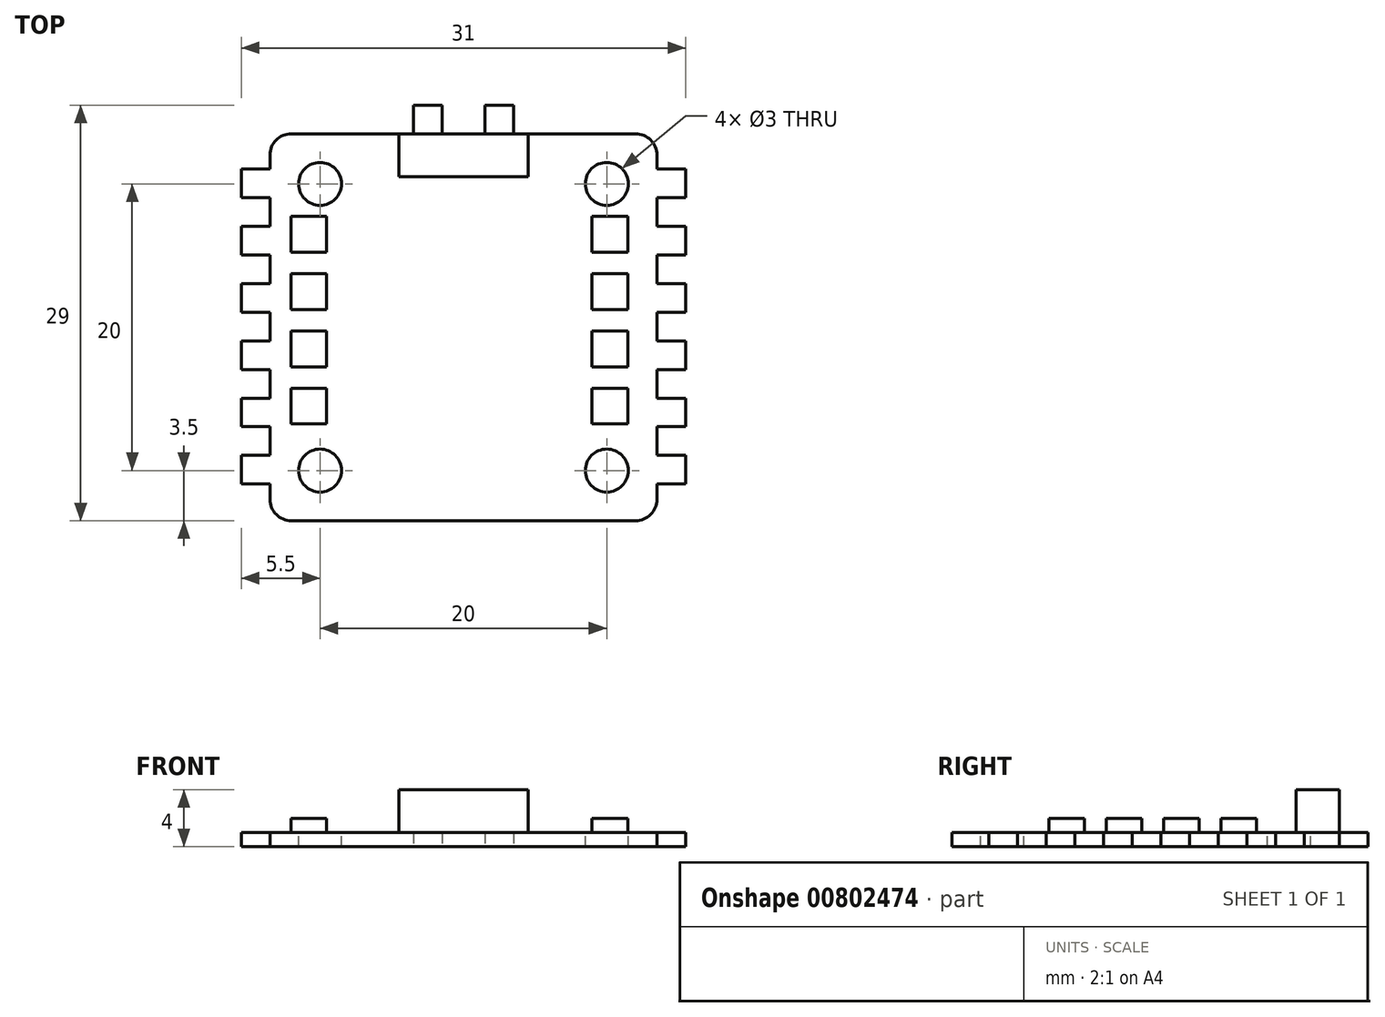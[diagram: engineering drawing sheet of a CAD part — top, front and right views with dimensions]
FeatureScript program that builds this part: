
annotation { "Feature Type Name" : "Feature", "Feature Type Description" : "" }
export const myFeature = defineFeature(function(context is Context, id is Id, definition is map)
    precondition{}
    {
        {
            var Q0;
            Q0=qCreatedBy(makeId("Top.planeOp"),FACE);
            var sketch = newSketch(context, id + "F0", { "sketchPlane" : qUnion([Q0])});
            skLineSegment(sketch, "E0.bottom", {"start": v(-12, 13.5) * mm, "end": v(12, 13.5) * mm});
            skLineSegment(sketch, "E0.top", {"start": v(-12, -13.5) * mm, "end": v(12, -13.5) * mm});
            skLineSegment(sketch, "E0.left", {"start": v(-13.5, 12) * mm, "end": v(-13.5, -12) * mm});
            skLineSegment(sketch, "E0.right", {"start": v(13.5, 12) * mm, "end": v(13.5, -12) * mm});
            skPoint(sketch, "E0.middle", {"position": v(0, 0) * mm});
            skPoint(sketch, "E1.visualSharp", {"position": v(-13.5, 13.5) * mm});
            skArc(sketch, "E1.filletArc", {"start": v(-12, 13.5) * mm, "mid": v(-13.06, 13.06) * mm, "end": v(-13.5, 12) * mm});
            skPoint(sketch, "E2.visualSharp", {"position": v(13.5, 13.5) * mm});
            skArc(sketch, "E2.filletArc", {"start": v(13.5, 12) * mm, "mid": v(13.06, 13.06) * mm, "end": v(12, 13.5) * mm});
            skPoint(sketch, "E3.visualSharp", {"position": v(13.5, -13.5) * mm});
            skArc(sketch, "E3.filletArc", {"start": v(12, -13.5) * mm, "mid": v(13.06, -13.06) * mm, "end": v(13.5, -12) * mm});
            skPoint(sketch, "E4.visualSharp", {"position": v(-13.5, -13.5) * mm});
            skArc(sketch, "E4.filletArc", {"start": v(-13.5, -12) * mm, "mid": v(-13.06, -13.06) * mm, "end": v(-12, -13.5) * mm});
            skLineSegment(sketch, "E5.bottom", {"start": v(-10, 10) * mm, "end": v(10, 10) * mm, "construction": true});
            skLineSegment(sketch, "E5.top", {"start": v(-10, -10) * mm, "end": v(10, -10) * mm, "construction": true});
            skLineSegment(sketch, "E5.left", {"start": v(-10, 10) * mm, "end": v(-10, -10) * mm, "construction": true});
            skLineSegment(sketch, "E5.right", {"start": v(10, 10) * mm, "end": v(10, -10) * mm, "construction": true});
            skPoint(sketch, "E6", {"position": v(-10, 10) * mm});
            skPoint(sketch, "E7", {"position": v(10, 10) * mm});
            skPoint(sketch, "E8", {"position": v(10, -10) * mm});
            skPoint(sketch, "E9", {"position": v(-10, -10) * mm});
            skSolve(sketch);
        }
        {
            var Q0;
            Q0=makeQuery(id+"F0.imprint","IMPRINT",FACE,{"disambiguationData":[TD([[makeQuery(id+"F0.imprint","IMPRINT",EDGE,{"derivedFrom":sQuery(id+"F0.wireOp",EDGE,"E0.bottom")}),-1.0]])]});
            extrude(context, id + "F1", {"entities" : qUnion([Q0]), "oppositeDirection" : true, "depth" : 1 * mm, "offsetDistance" : 25 * mm});
        }
        {
            var Q0;
            Q0=sQuery(id+"F0.wireOp",VERTEX,"E6");
            var Q1;
            Q1=sQuery(id+"F0.wireOp",VERTEX,"E7");
            var Q2;
            Q2=sQuery(id+"F0.wireOp",VERTEX,"E8");
            var Q3;
            Q3=sQuery(id+"F0.wireOp",VERTEX,"E9");
            var Q4;
            Q4=makeQuery(id+"F1.opExtrude","SWEPT_BODY",BODY,{"disambiguationData":[OSD([sQuery(id+"F0.wireOp",EDGE,"E0.bottom"),sQuery(id+"F0.wireOp",EDGE,"E0.top"),sQuery(id+"F0.wireOp",EDGE,"E0.left"),sQuery(id+"F0.wireOp",EDGE,"E0.right"),sQuery(id+"F0.wireOp",EDGE,"E1.filletArc"),sQuery(id+"F0.wireOp",EDGE,"E2.filletArc"),sQuery(id+"F0.wireOp",EDGE,"E3.filletArc"),sQuery(id+"F0.wireOp",EDGE,"E4.filletArc")])]});
            hole(context, id + "F2", {"style" : HoleStyle.SIMPLE, "endStyle" : HoleEndStyle.BLIND, "holeDiameter" : 3 * mm, "majorDiameter" : 5 * mm, "holeDepth" : 5 * mm, "isTappedThrough" : true, "tappedDepth" : 12 * mm, "tapClearance" : 3, "locations" : qUnion([Q0, Q1, Q2, Q3]), "scope" : qUnion([Q4])});
        }
        {
            var Q0;
            Q0=makeQuery(id+"F1.opExtrude","CAP_FACE",FACE,{"disambiguationData":[OSD([sQuery(id+"F0.wireOp",EDGE,"E0.bottom"),sQuery(id+"F0.wireOp",EDGE,"E0.top"),sQuery(id+"F0.wireOp",EDGE,"E0.left"),sQuery(id+"F0.wireOp",EDGE,"E0.right"),sQuery(id+"F0.wireOp",EDGE,"E1.filletArc"),sQuery(id+"F0.wireOp",EDGE,"E2.filletArc"),sQuery(id+"F0.wireOp",EDGE,"E3.filletArc"),sQuery(id+"F0.wireOp",EDGE,"E4.filletArc")])],"isStart":false});
            var sketch = newSketch(context, id + "F3", { "sketchPlane" : qUnion([Q0])});
            skLineSegment(sketch, "E10.bottom", {"start": v(-13.5, 10.94) * mm, "end": v(-15.5, 10.94) * mm});
            skLineSegment(sketch, "E10.top", {"start": v(-13.5, 8.94) * mm, "end": v(-15.5, 8.94) * mm});
            skLineSegment(sketch, "E10.left", {"start": v(-13.5, 10.94) * mm, "end": v(-13.5, 8.94) * mm});
            skLineSegment(sketch, "E10.right", {"start": v(-15.5, 10.94) * mm, "end": v(-15.5, 8.94) * mm});
            skLineSegment(sketch, "E11.0.1.0", {"start": v(-13.5, 6.94) * mm, "end": v(-15.5, 6.94) * mm});
            skLineSegment(sketch, "E11.0.1.1", {"start": v(-13.5, 4.94) * mm, "end": v(-15.5, 4.94) * mm});
            skLineSegment(sketch, "E11.0.1.2", {"start": v(-13.5, 6.94) * mm, "end": v(-13.5, 4.94) * mm});
            skLineSegment(sketch, "E11.0.1.3", {"start": v(-15.5, 6.94) * mm, "end": v(-15.5, 4.94) * mm});
            skLineSegment(sketch, "E11.0.2.0", {"start": v(-13.5, 2.94) * mm, "end": v(-15.5, 2.94) * mm});
            skLineSegment(sketch, "E11.0.2.1", {"start": v(-13.5, 0.94) * mm, "end": v(-15.5, 0.94) * mm});
            skLineSegment(sketch, "E11.0.2.2", {"start": v(-13.5, 2.94) * mm, "end": v(-13.5, 0.94) * mm});
            skLineSegment(sketch, "E11.0.2.3", {"start": v(-15.5, 2.94) * mm, "end": v(-15.5, 0.94) * mm});
            skLineSegment(sketch, "E11.0.3.0", {"start": v(-13.5, -1.06) * mm, "end": v(-15.5, -1.06) * mm});
            skLineSegment(sketch, "E11.0.3.1", {"start": v(-13.5, -3.06) * mm, "end": v(-15.5, -3.06) * mm});
            skLineSegment(sketch, "E11.0.3.2", {"start": v(-13.5, -1.06) * mm, "end": v(-13.5, -3.06) * mm});
            skLineSegment(sketch, "E11.0.3.3", {"start": v(-15.5, -1.06) * mm, "end": v(-15.5, -3.06) * mm});
            skLineSegment(sketch, "E11.0.4.0", {"start": v(-13.5, -5.06) * mm, "end": v(-15.5, -5.06) * mm});
            skLineSegment(sketch, "E11.0.4.1", {"start": v(-13.5, -7.06) * mm, "end": v(-15.5, -7.06) * mm});
            skLineSegment(sketch, "E11.0.4.2", {"start": v(-13.5, -5.06) * mm, "end": v(-13.5, -7.06) * mm});
            skLineSegment(sketch, "E11.0.4.3", {"start": v(-15.5, -5.06) * mm, "end": v(-15.5, -7.06) * mm});
            skLineSegment(sketch, "E11.0.5.0", {"start": v(-13.5, -9.06) * mm, "end": v(-15.5, -9.06) * mm});
            skLineSegment(sketch, "E11.0.5.1", {"start": v(-13.5, -11.06) * mm, "end": v(-15.5, -11.06) * mm});
            skLineSegment(sketch, "E11.0.5.2", {"start": v(-13.5, -9.06) * mm, "end": v(-13.5, -11.06) * mm});
            skLineSegment(sketch, "E11.0.5.3", {"start": v(-15.5, -9.06) * mm, "end": v(-15.5, -11.06) * mm});
            skLineSegment(sketch, "E11.1.0.0", {"start": v(15.5, 10.94) * mm, "end": v(13.5, 10.94) * mm});
            skLineSegment(sketch, "E11.1.0.1", {"start": v(15.5, 8.94) * mm, "end": v(13.5, 8.94) * mm});
            skLineSegment(sketch, "E11.1.0.2", {"start": v(15.5, 10.94) * mm, "end": v(15.5, 8.94) * mm});
            skLineSegment(sketch, "E11.1.0.3", {"start": v(13.5, 10.94) * mm, "end": v(13.5, 8.94) * mm});
            skLineSegment(sketch, "E11.1.1.0", {"start": v(15.5, 6.94) * mm, "end": v(13.5, 6.94) * mm});
            skLineSegment(sketch, "E11.1.1.1", {"start": v(15.5, 4.94) * mm, "end": v(13.5, 4.94) * mm});
            skLineSegment(sketch, "E11.1.1.2", {"start": v(15.5, 6.94) * mm, "end": v(15.5, 4.94) * mm});
            skLineSegment(sketch, "E11.1.1.3", {"start": v(13.5, 6.94) * mm, "end": v(13.5, 4.94) * mm});
            skLineSegment(sketch, "E11.1.2.0", {"start": v(15.5, 2.94) * mm, "end": v(13.5, 2.94) * mm});
            skLineSegment(sketch, "E11.1.2.1", {"start": v(15.5, 0.94) * mm, "end": v(13.5, 0.94) * mm});
            skLineSegment(sketch, "E11.1.2.2", {"start": v(15.5, 2.94) * mm, "end": v(15.5, 0.94) * mm});
            skLineSegment(sketch, "E11.1.2.3", {"start": v(13.5, 2.94) * mm, "end": v(13.5, 0.94) * mm});
            skLineSegment(sketch, "E11.1.3.0", {"start": v(15.5, -1.06) * mm, "end": v(13.5, -1.06) * mm});
            skLineSegment(sketch, "E11.1.3.1", {"start": v(15.5, -3.06) * mm, "end": v(13.5, -3.06) * mm});
            skLineSegment(sketch, "E11.1.3.2", {"start": v(15.5, -1.06) * mm, "end": v(15.5, -3.06) * mm});
            skLineSegment(sketch, "E11.1.3.3", {"start": v(13.5, -1.06) * mm, "end": v(13.5, -3.06) * mm});
            skLineSegment(sketch, "E11.1.4.0", {"start": v(15.5, -5.06) * mm, "end": v(13.5, -5.06) * mm});
            skLineSegment(sketch, "E11.1.4.1", {"start": v(15.5, -7.06) * mm, "end": v(13.5, -7.06) * mm});
            skLineSegment(sketch, "E11.1.4.2", {"start": v(15.5, -5.06) * mm, "end": v(15.5, -7.06) * mm});
            skLineSegment(sketch, "E11.1.4.3", {"start": v(13.5, -5.06) * mm, "end": v(13.5, -7.06) * mm});
            skLineSegment(sketch, "E11.1.5.0", {"start": v(15.5, -9.06) * mm, "end": v(13.5, -9.06) * mm});
            skLineSegment(sketch, "E11.1.5.1", {"start": v(15.5, -11.06) * mm, "end": v(13.5, -11.06) * mm});
            skLineSegment(sketch, "E11.1.5.2", {"start": v(15.5, -9.06) * mm, "end": v(15.5, -11.06) * mm});
            skLineSegment(sketch, "E11.1.5.3", {"start": v(13.5, -9.06) * mm, "end": v(13.5, -11.06) * mm});
            skLineSegment(sketch, "E11.direction1", {"start": v(-15.5, 8.94) * mm, "end": v(13.5, 8.94) * mm, "construction": true});
            skLineSegment(sketch, "E11.direction2", {"start": v(-15.5, 8.94) * mm, "end": v(-15.5, 4.94) * mm, "construction": true});
            skLineSegment(sketch, "E12.bottom", {"start": v(-1.5, -13.5) * mm, "end": v(-3.5, -13.5) * mm});
            skLineSegment(sketch, "E12.top", {"start": v(-1.5, -15.5) * mm, "end": v(-3.5, -15.5) * mm});
            skLineSegment(sketch, "E12.left", {"start": v(-1.5, -13.5) * mm, "end": v(-1.5, -15.5) * mm});
            skLineSegment(sketch, "E12.right", {"start": v(-3.5, -13.5) * mm, "end": v(-3.5, -15.5) * mm});
            skLineSegment(sketch, "E13.MirrorCS", {"start": v(1.5, -13.5) * mm, "end": v(3.5, -13.5) * mm});
            skLineSegment(sketch, "E14.MirrorCS", {"start": v(1.5, -15.5) * mm, "end": v(3.5, -15.5) * mm});
            skLineSegment(sketch, "E15.MirrorCS", {"start": v(3.5, -13.5) * mm, "end": v(3.5, -15.5) * mm});
            skLineSegment(sketch, "E16.MirrorCS", {"start": v(1.5, -13.5) * mm, "end": v(1.5, -15.5) * mm});
            skSolve(sketch);
        }
        {
            var Q0;
            Q0=makeQuery(id+"F3.imprint","IMPRINT",FACE,{"disambiguationData":[TD([[makeQuery(id+"F3.imprint","IMPRINT",EDGE,{"derivedFrom":sQuery(id+"F3.wireOp",EDGE,"E10.bottom")}),1.0]])]});
            var Q1;
            Q1=makeQuery(id+"F3.imprint","IMPRINT",FACE,{"disambiguationData":[TD([[makeQuery(id+"F3.imprint","IMPRINT",EDGE,{"derivedFrom":sQuery(id+"F3.wireOp",EDGE,"E11.0.1.0")}),1.0]])]});
            var Q2;
            Q2=makeQuery(id+"F3.imprint","IMPRINT",FACE,{"disambiguationData":[TD([[makeQuery(id+"F3.imprint","IMPRINT",EDGE,{"derivedFrom":sQuery(id+"F3.wireOp",EDGE,"E11.0.2.0")}),1.0]])]});
            var Q3;
            Q3=makeQuery(id+"F3.imprint","IMPRINT",FACE,{"disambiguationData":[TD([[makeQuery(id+"F3.imprint","IMPRINT",EDGE,{"derivedFrom":sQuery(id+"F3.wireOp",EDGE,"E11.0.3.0")}),1.0]])]});
            var Q4;
            Q4=makeQuery(id+"F3.imprint","IMPRINT",FACE,{"disambiguationData":[TD([[makeQuery(id+"F3.imprint","IMPRINT",EDGE,{"derivedFrom":sQuery(id+"F3.wireOp",EDGE,"E11.0.4.0")}),1.0]])]});
            var Q5;
            Q5=makeQuery(id+"F3.imprint","IMPRINT",FACE,{"disambiguationData":[TD([[makeQuery(id+"F3.imprint","IMPRINT",EDGE,{"derivedFrom":sQuery(id+"F3.wireOp",EDGE,"E11.0.5.0")}),1.0]])]});
            var Q6;
            Q6=makeQuery(id+"F3.imprint","IMPRINT",FACE,{"disambiguationData":[TD([[makeQuery(id+"F3.imprint","IMPRINT",EDGE,{"derivedFrom":sQuery(id+"F3.wireOp",EDGE,"E11.1.0.0")}),1.0]])]});
            var Q7;
            Q7=makeQuery(id+"F3.imprint","IMPRINT",FACE,{"disambiguationData":[TD([[makeQuery(id+"F3.imprint","IMPRINT",EDGE,{"derivedFrom":sQuery(id+"F3.wireOp",EDGE,"E11.1.1.0")}),1.0]])]});
            var Q8;
            Q8=makeQuery(id+"F3.imprint","IMPRINT",FACE,{"disambiguationData":[TD([[makeQuery(id+"F3.imprint","IMPRINT",EDGE,{"derivedFrom":sQuery(id+"F3.wireOp",EDGE,"E11.1.2.0")}),1.0]])]});
            var Q9;
            Q9=makeQuery(id+"F3.imprint","IMPRINT",FACE,{"disambiguationData":[TD([[makeQuery(id+"F3.imprint","IMPRINT",EDGE,{"derivedFrom":sQuery(id+"F3.wireOp",EDGE,"E11.1.3.0")}),1.0]])]});
            var Q10;
            Q10=makeQuery(id+"F3.imprint","IMPRINT",FACE,{"disambiguationData":[TD([[makeQuery(id+"F3.imprint","IMPRINT",EDGE,{"derivedFrom":sQuery(id+"F3.wireOp",EDGE,"E11.1.4.0")}),1.0]])]});
            var Q11;
            Q11=makeQuery(id+"F3.imprint","IMPRINT",FACE,{"disambiguationData":[TD([[makeQuery(id+"F3.imprint","IMPRINT",EDGE,{"derivedFrom":sQuery(id+"F3.wireOp",EDGE,"E11.1.5.0")}),1.0]])]});
            var Q12;
            Q12=makeQuery(id+"F3.imprint","IMPRINT",FACE,{"disambiguationData":[TD([[makeQuery(id+"F3.imprint","IMPRINT",EDGE,{"derivedFrom":sQuery(id+"F3.wireOp",EDGE,"E12.bottom")}),-1.0]])]});
            var Q13;
            Q13=makeQuery(id+"F3.imprint","IMPRINT",FACE,{"disambiguationData":[TD([[makeQuery(id+"F3.imprint","IMPRINT",EDGE,{"derivedFrom":sQuery(id+"F3.wireOp",EDGE,"E13.MirrorCS")}),-1.0]])]});
            extrude(context, id + "F4", {"entities" : qUnion([Q0, Q1, Q2, Q3, Q4, Q5, Q6, Q7, Q8, Q9, Q10, Q11, Q12, Q13]), "operationType" : NewBodyOperationType.ADD, "oppositeDirection" : true, "depth" : 1 * mm, "offsetDistance" : 25 * mm});
        }
        {
            var Q0;
            Q0=makeQuery(id+"F0.imprint","IMPRINT",FACE,{"disambiguationData":[TD([[makeQuery(id+"F0.imprint","IMPRINT",EDGE,{"derivedFrom":sQuery(id+"F0.wireOp",EDGE,"E0.bottom")}),-1.0]])]});
            var sketch = newSketch(context, id + "F5", { "sketchPlane" : qUnion([Q0])});
            skLineSegment(sketch, "E17.bottom", {"start": v(-4.5, 13.5) * mm, "end": v(4.5, 13.5) * mm});
            skLineSegment(sketch, "E17.top", {"start": v(-4.5, 10.5) * mm, "end": v(4.5, 10.5) * mm});
            skLineSegment(sketch, "E17.left", {"start": v(-4.5, 13.5) * mm, "end": v(-4.5, 10.5) * mm});
            skLineSegment(sketch, "E17.right", {"start": v(4.5, 13.5) * mm, "end": v(4.5, 10.5) * mm});
            skSolve(sketch);
        }
        {
            var Q0;
            Q0=makeQuery(id+"F5.imprint","IMPRINT",FACE,{"disambiguationData":[TD([[makeQuery(id+"F5.imprint","IMPRINT",EDGE,{"derivedFrom":sQuery(id+"F5.wireOp",EDGE,"E17.bottom")}),-1.0]])]});
            extrude(context, id + "F6", {"entities" : qUnion([Q0]), "operationType" : NewBodyOperationType.ADD, "depth" : 3 * mm, "offsetDistance" : 25 * mm});
        }
        {
            var Q0;
            {var subQ0=sQuery(id+"F3.wireOp",EDGE,"E11.1.5.0");var subQ1=sQuery(id+"F3.wireOp",EDGE,"E11.1.4.1");var subQ2=sQuery(id+"F0.wireOp",EDGE,"E2.filletArc");var subQ3=sQuery(id+"F3.wireOp",EDGE,"E11.1.4.0");var subQ4=sQuery(id+"F0.wireOp",EDGE,"E0.left");var subQ5=sQuery(id+"F3.wireOp",EDGE,"E11.1.3.0");var subQ6=sQuery(id+"F3.wireOp",EDGE,"E11.1.2.1");var subQ7=sQuery(id+"F3.wireOp",EDGE,"E11.1.2.0");var subQ8=sQuery(id+"F3.wireOp",EDGE,"E11.1.1.2");var subQ9=sQuery(id+"F3.wireOp",EDGE,"E11.0.5.3");var subQ10=sQuery(id+"F3.wireOp",EDGE,"E11.0.5.1");var subQ11=sQuery(id+"F3.wireOp",EDGE,"E11.0.5.0");var subQ12=sQuery(id+"F3.wireOp",EDGE,"E11.0.4.3");var subQ13=sQuery(id+"F3.wireOp",EDGE,"E11.0.4.1");var subQ14=sQuery(id+"F3.wireOp",EDGE,"E11.0.4.0");var subQ15=sQuery(id+"F3.wireOp",EDGE,"E11.0.3.3");var subQ16=sQuery(id+"F3.wireOp",EDGE,"E11.0.3.1");var subQ17=sQuery(id+"F3.wireOp",EDGE,"E11.1.1.1");var subQ18=sQuery(id+"F0.wireOp",EDGE,"E4.filletArc");var subQ19=sQuery(id+"F3.wireOp",EDGE,"E11.0.1.1");var subQ20=sQuery(id+"F0.wireOp",EDGE,"E3.filletArc");var subQ21=sQuery(id+"F3.wireOp",EDGE,"E11.1.4.2");var subQ22=sQuery(id+"F3.wireOp",EDGE,"E11.0.1.0");var subQ23=sQuery(id+"F3.wireOp",EDGE,"E11.1.0.0");var subQ24=sQuery(id+"F0.wireOp",EDGE,"E0.bottom");var subQ25=sQuery(id+"F3.wireOp",EDGE,"E10.bottom");var subQ26=sQuery(id+"F3.wireOp",EDGE,"E11.1.1.0");var subQ27=sQuery(id+"F0.wireOp",EDGE,"E1.filletArc");var subQ28=sQuery(id+"F3.wireOp",EDGE,"E11.1.2.2");var subQ29=sQuery(id+"F3.wireOp",EDGE,"E10.right");var subQ30=sQuery(id+"F3.wireOp",EDGE,"E11.0.2.0");var subQ31=sQuery(id+"F3.wireOp",EDGE,"E11.1.0.1");var subQ32=sQuery(id+"F0.wireOp",EDGE,"E0.top");var subQ33=sQuery(id+"F3.wireOp",EDGE,"E10.top");var subQ34=sQuery(id+"F3.wireOp",EDGE,"E11.1.0.2");var subQ35=sQuery(id+"F3.wireOp",EDGE,"E11.1.3.1");var subQ36=sQuery(id+"F3.wireOp",EDGE,"E11.1.3.2");var subQ37=sQuery(id+"F3.wireOp",EDGE,"E11.0.1.3");var subQ38=sQuery(id+"F0.wireOp",EDGE,"E0.right");var subQ39=sQuery(id+"F3.wireOp",EDGE,"E11.0.2.1");var subQ40=sQuery(id+"F3.wireOp",EDGE,"E11.0.2.3");var subQ41=sQuery(id+"F3.wireOp",EDGE,"E11.0.3.0");var subQ42=sQuery(id+"F3.wireOp",EDGE,"E11.1.5.1");var subQ43=sQuery(id+"F3.wireOp",EDGE,"E11.1.5.2");Q0=makeQuery(id+"F6.boolean.opBoolean","SPLIT",FACE,{"disambiguationData":[TD([makeQuery(id+"F1.opExtrude","SWEPT_FACE",FACE,{"disambiguationData":[OSD([subQ32])]})])],"derivedFrom":makeQuery(id+"F4.boolean.opBoolean","MERGE",FACE,{"derivedFrom":[makeQuery(id+"F1.opExtrude","CAP_FACE",FACE,{"disambiguationData":[OSD([subQ24,subQ32,subQ4,subQ38,subQ27,subQ2,subQ20,subQ18])],"isStart":true}),makeQuery(id+"F4.opExtrude","CAP_FACE",FACE,{"disambiguationData":[OSD([subQ25,subQ33,sQuery(id+"F3.wireOp",EDGE,"E10.left"),subQ29])],"isStart":false}),makeQuery(id+"F4.opExtrude","CAP_FACE",FACE,{"disambiguationData":[OSD([subQ22,subQ19,sQuery(id+"F3.wireOp",EDGE,"E11.0.1.2"),subQ37])],"isStart":false}),makeQuery(id+"F4.opExtrude","CAP_FACE",FACE,{"disambiguationData":[OSD([subQ30,subQ39,sQuery(id+"F3.wireOp",EDGE,"E11.0.2.2"),subQ40])],"isStart":false}),makeQuery(id+"F4.opExtrude","CAP_FACE",FACE,{"disambiguationData":[OSD([subQ41,subQ16,sQuery(id+"F3.wireOp",EDGE,"E11.0.3.2"),subQ15])],"isStart":false}),makeQuery(id+"F4.opExtrude","CAP_FACE",FACE,{"disambiguationData":[OSD([subQ14,subQ13,sQuery(id+"F3.wireOp",EDGE,"E11.0.4.2"),subQ12])],"isStart":false}),makeQuery(id+"F4.opExtrude","CAP_FACE",FACE,{"disambiguationData":[OSD([subQ11,subQ10,sQuery(id+"F3.wireOp",EDGE,"E11.0.5.2"),subQ9])],"isStart":false}),makeQuery(id+"F4.opExtrude","CAP_FACE",FACE,{"disambiguationData":[OSD([subQ23,subQ31,subQ34,sQuery(id+"F3.wireOp",EDGE,"E11.1.0.3")])],"isStart":false}),makeQuery(id+"F4.opExtrude","CAP_FACE",FACE,{"disambiguationData":[OSD([subQ26,subQ17,subQ8,sQuery(id+"F3.wireOp",EDGE,"E11.1.1.3")])],"isStart":false}),makeQuery(id+"F4.opExtrude","CAP_FACE",FACE,{"disambiguationData":[OSD([subQ7,subQ6,subQ28,sQuery(id+"F3.wireOp",EDGE,"E11.1.2.3")])],"isStart":false}),makeQuery(id+"F4.opExtrude","CAP_FACE",FACE,{"disambiguationData":[OSD([subQ5,subQ35,subQ36,sQuery(id+"F3.wireOp",EDGE,"E11.1.3.3")])],"isStart":false}),makeQuery(id+"F4.opExtrude","CAP_FACE",FACE,{"disambiguationData":[OSD([subQ3,subQ1,subQ21,sQuery(id+"F3.wireOp",EDGE,"E11.1.4.3")])],"isStart":false}),makeQuery(id+"F4.opExtrude","CAP_FACE",FACE,{"disambiguationData":[OSD([subQ0,subQ42,subQ43,sQuery(id+"F3.wireOp",EDGE,"E11.1.5.3")])],"isStart":false}),makeQuery(id+"F4.opExtrude","CAP_FACE",FACE,{"disambiguationData":[OSD([sQuery(id+"F3.wireOp",EDGE,"E12.bottom"),sQuery(id+"F3.wireOp",EDGE,"E12.top"),sQuery(id+"F3.wireOp",EDGE,"E12.left"),sQuery(id+"F3.wireOp",EDGE,"E12.right")])],"isStart":false}),makeQuery(id+"F4.opExtrude","CAP_FACE",FACE,{"disambiguationData":[OSD([sQuery(id+"F3.wireOp",EDGE,"E13.MirrorCS"),sQuery(id+"F3.wireOp",EDGE,"E14.MirrorCS"),sQuery(id+"F3.wireOp",EDGE,"E15.MirrorCS"),sQuery(id+"F3.wireOp",EDGE,"E16.MirrorCS")])],"isStart":false})]})});}
            var sketch = newSketch(context, id + "F7", { "sketchPlane" : qUnion([Q0])});
            skLineSegment(sketch, "E18.bottom", {"start": v(-9.54, 7.75) * mm, "end": v(-12.04, 7.75) * mm});
            skLineSegment(sketch, "E18.top", {"start": v(-9.54, 5.25) * mm, "end": v(-12.04, 5.25) * mm});
            skLineSegment(sketch, "E18.left", {"start": v(-9.54, 7.75) * mm, "end": v(-9.54, 5.25) * mm});
            skLineSegment(sketch, "E18.right", {"start": v(-12.04, 7.75) * mm, "end": v(-12.04, 5.25) * mm});
            skPoint(sketch, "E18.middle", {"position": v(-10.79, 6.5) * mm});
            skPoint(sketch, "E19.0.1.0", {"position": v(-10.79, 2.5) * mm});
            skLineSegment(sketch, "E19.0.1.1", {"start": v(-12.04, 3.75) * mm, "end": v(-12.04, 1.25) * mm});
            skLineSegment(sketch, "E19.0.1.2", {"start": v(-9.54, 3.75) * mm, "end": v(-9.54, 1.25) * mm});
            skLineSegment(sketch, "E19.0.1.3", {"start": v(-9.54, 1.25) * mm, "end": v(-12.04, 1.25) * mm});
            skLineSegment(sketch, "E19.0.1.4", {"start": v(-9.54, 3.75) * mm, "end": v(-12.04, 3.75) * mm});
            skPoint(sketch, "E19.0.2.0", {"position": v(-10.79, -1.5) * mm});
            skLineSegment(sketch, "E19.0.2.1", {"start": v(-12.04, -0.25) * mm, "end": v(-12.04, -2.75) * mm});
            skLineSegment(sketch, "E19.0.2.2", {"start": v(-9.54, -0.25) * mm, "end": v(-9.54, -2.75) * mm});
            skLineSegment(sketch, "E19.0.2.3", {"start": v(-9.54, -2.75) * mm, "end": v(-12.04, -2.75) * mm});
            skLineSegment(sketch, "E19.0.2.4", {"start": v(-9.54, -0.25) * mm, "end": v(-12.04, -0.25) * mm});
            skPoint(sketch, "E19.0.3.0", {"position": v(-10.79, -5.5) * mm});
            skLineSegment(sketch, "E19.0.3.1", {"start": v(-12.04, -4.25) * mm, "end": v(-12.04, -6.75) * mm});
            skLineSegment(sketch, "E19.0.3.2", {"start": v(-9.54, -4.25) * mm, "end": v(-9.54, -6.75) * mm});
            skLineSegment(sketch, "E19.0.3.3", {"start": v(-9.54, -6.75) * mm, "end": v(-12.04, -6.75) * mm});
            skLineSegment(sketch, "E19.0.3.4", {"start": v(-9.54, -4.25) * mm, "end": v(-12.04, -4.25) * mm});
            skPoint(sketch, "E19.1.0.0", {"position": v(10.21, 6.5) * mm});
            skLineSegment(sketch, "E19.1.0.1", {"start": v(8.96, 7.75) * mm, "end": v(8.96, 5.25) * mm});
            skLineSegment(sketch, "E19.1.0.2", {"start": v(11.46, 7.75) * mm, "end": v(11.46, 5.25) * mm});
            skLineSegment(sketch, "E19.1.0.3", {"start": v(11.46, 5.25) * mm, "end": v(8.96, 5.25) * mm});
            skLineSegment(sketch, "E19.1.0.4", {"start": v(11.46, 7.75) * mm, "end": v(8.96, 7.75) * mm});
            skPoint(sketch, "E19.1.1.0", {"position": v(10.21, 2.5) * mm});
            skLineSegment(sketch, "E19.1.1.1", {"start": v(8.96, 3.75) * mm, "end": v(8.96, 1.25) * mm});
            skLineSegment(sketch, "E19.1.1.2", {"start": v(11.46, 3.75) * mm, "end": v(11.46, 1.25) * mm});
            skLineSegment(sketch, "E19.1.1.3", {"start": v(11.46, 1.25) * mm, "end": v(8.96, 1.25) * mm});
            skLineSegment(sketch, "E19.1.1.4", {"start": v(11.46, 3.75) * mm, "end": v(8.96, 3.75) * mm});
            skPoint(sketch, "E19.1.2.0", {"position": v(10.21, -1.5) * mm});
            skLineSegment(sketch, "E19.1.2.1", {"start": v(8.96, -0.25) * mm, "end": v(8.96, -2.75) * mm});
            skLineSegment(sketch, "E19.1.2.2", {"start": v(11.46, -0.25) * mm, "end": v(11.46, -2.75) * mm});
            skLineSegment(sketch, "E19.1.2.3", {"start": v(11.46, -2.75) * mm, "end": v(8.96, -2.75) * mm});
            skLineSegment(sketch, "E19.1.2.4", {"start": v(11.46, -0.25) * mm, "end": v(8.96, -0.25) * mm});
            skPoint(sketch, "E19.1.3.0", {"position": v(10.21, -5.5) * mm});
            skLineSegment(sketch, "E19.1.3.1", {"start": v(8.96, -4.25) * mm, "end": v(8.96, -6.75) * mm});
            skLineSegment(sketch, "E19.1.3.2", {"start": v(11.46, -4.25) * mm, "end": v(11.46, -6.75) * mm});
            skLineSegment(sketch, "E19.1.3.3", {"start": v(11.46, -6.75) * mm, "end": v(8.96, -6.75) * mm});
            skLineSegment(sketch, "E19.1.3.4", {"start": v(11.46, -4.25) * mm, "end": v(8.96, -4.25) * mm});
            skLineSegment(sketch, "E19.direction1", {"start": v(-12.04, 5.25) * mm, "end": v(8.96, 5.25) * mm, "construction": true});
            skLineSegment(sketch, "E19.direction2", {"start": v(-12.04, 5.25) * mm, "end": v(-12.04, 1.25) * mm, "construction": true});
            skSolve(sketch);
        }
        {
            var Q0;
            Q0=makeQuery(id+"F7.imprint","IMPRINT",FACE,{"disambiguationData":[TD([[makeQuery(id+"F7.imprint","IMPRINT",EDGE,{"derivedFrom":sQuery(id+"F7.wireOp",EDGE,"E19.0.1.1")}),1.0]])]});
            var Q1;
            Q1=makeQuery(id+"F7.imprint","IMPRINT",FACE,{"disambiguationData":[TD([[makeQuery(id+"F7.imprint","IMPRINT",EDGE,{"derivedFrom":sQuery(id+"F7.wireOp",EDGE,"E19.0.2.1")}),1.0]])]});
            var Q2;
            Q2=makeQuery(id+"F7.imprint","IMPRINT",FACE,{"disambiguationData":[TD([[makeQuery(id+"F7.imprint","IMPRINT",EDGE,{"derivedFrom":sQuery(id+"F7.wireOp",EDGE,"E19.0.3.1")}),1.0]])]});
            var Q3;
            Q3=makeQuery(id+"F7.imprint","IMPRINT",FACE,{"disambiguationData":[TD([[makeQuery(id+"F7.imprint","IMPRINT",EDGE,{"derivedFrom":sQuery(id+"F7.wireOp",EDGE,"E18.bottom")}),1.0]])]});
            var Q4;
            Q4=makeQuery(id+"F7.imprint","IMPRINT",FACE,{"disambiguationData":[TD([[makeQuery(id+"F7.imprint","IMPRINT",EDGE,{"derivedFrom":sQuery(id+"F7.wireOp",EDGE,"E19.1.0.1")}),1.0]])]});
            var Q5;
            Q5=makeQuery(id+"F7.imprint","IMPRINT",FACE,{"disambiguationData":[TD([[makeQuery(id+"F7.imprint","IMPRINT",EDGE,{"derivedFrom":sQuery(id+"F7.wireOp",EDGE,"E19.1.1.1")}),1.0]])]});
            var Q6;
            Q6=makeQuery(id+"F7.imprint","IMPRINT",FACE,{"disambiguationData":[TD([[makeQuery(id+"F7.imprint","IMPRINT",EDGE,{"derivedFrom":sQuery(id+"F7.wireOp",EDGE,"E19.1.2.1")}),1.0]])]});
            var Q7;
            Q7=makeQuery(id+"F7.imprint","IMPRINT",FACE,{"disambiguationData":[TD([[makeQuery(id+"F7.imprint","IMPRINT",EDGE,{"derivedFrom":sQuery(id+"F7.wireOp",EDGE,"E19.1.3.1")}),1.0]])]});
            extrude(context, id + "F8", {"entities" : qUnion([Q0, Q1, Q2, Q3, Q4, Q5, Q6, Q7]), "operationType" : NewBodyOperationType.ADD, "depth" : 1 * mm, "offsetDistance" : 25 * mm});
        }
    });
